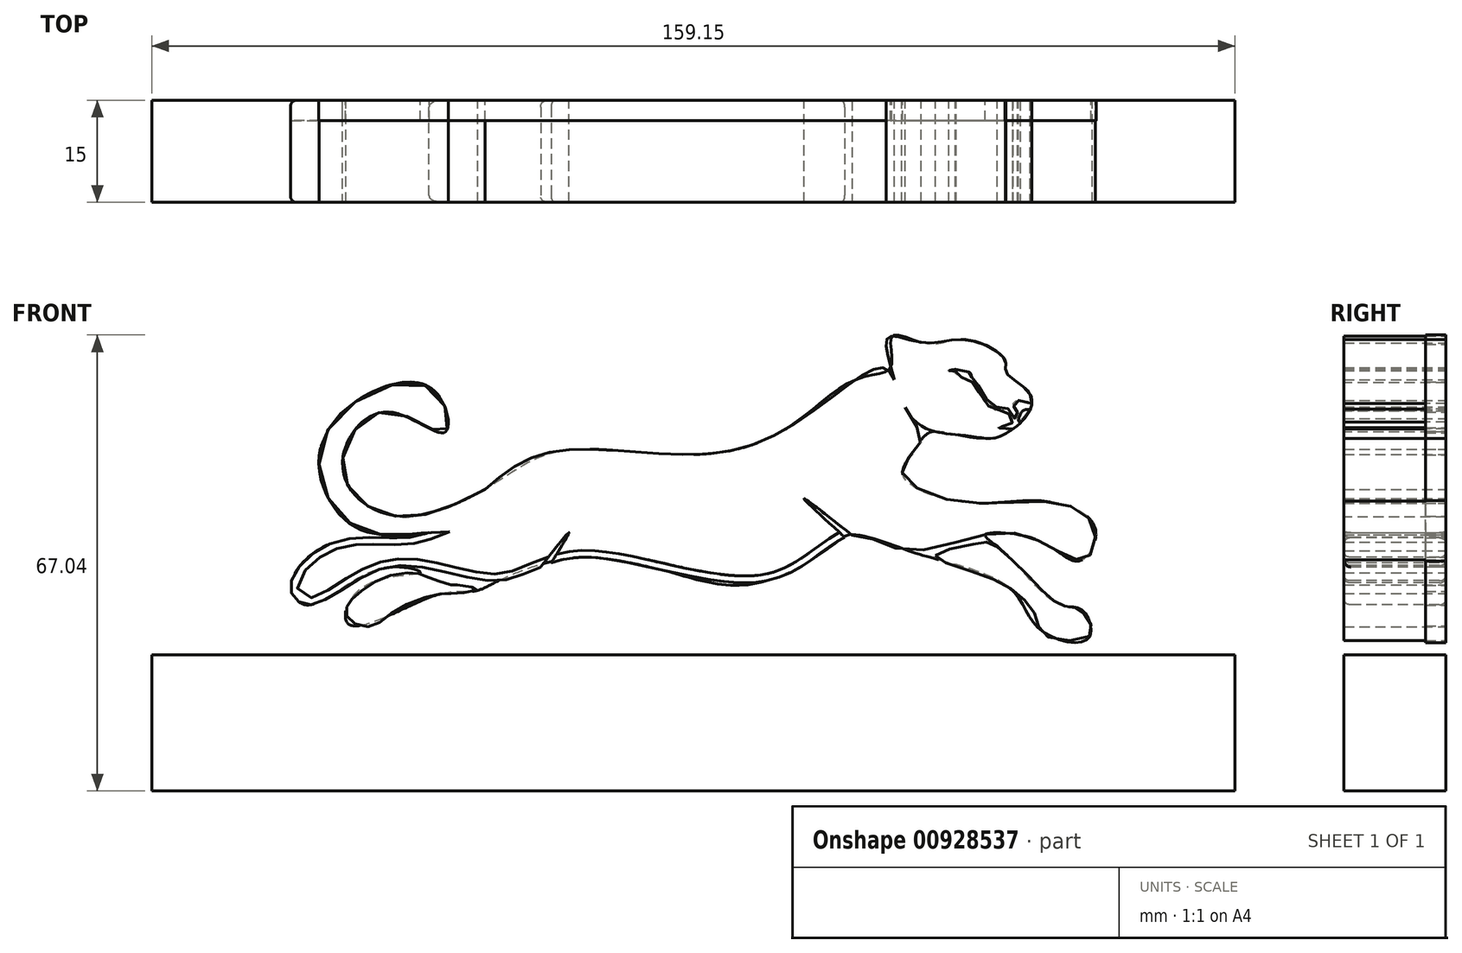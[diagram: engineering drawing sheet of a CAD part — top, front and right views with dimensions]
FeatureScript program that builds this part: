
annotation { "Feature Type Name" : "Feature", "Feature Type Description" : "" }
export const myFeature = defineFeature(function(context is Context, id is Id, definition is map)
    precondition{}
    {
        {
            var Q0;
            Q0=qCreatedBy(makeId("Front.planeOp"),FACE);
            var sketch = newSketch(context, id + "F0", { "sketchPlane" : qUnion([Q0])});
            skFitSpline(sketch, "E0", {"points": [v(-30.14, 6.91) * mm, v(-9.5, 13.73) * mm, v(10.97, 13.73) * mm, v(29.59, 25.16) * mm], "startDerivative": vector(60.52, 28) * mm, "endDerivative": vector(53.1, 44.41) * mm});
            skFitSpline(sketch, "E1", {"points": [v(-23.36, 10.05) * mm, v(-23.36, 18.53) * mm], "startDerivative": vector(0, 8.47) * mm, "endDerivative": vector(0, 8.47) * mm});
            skFitSpline(sketch, "E2", {"points": [v(-49.89, 46.42) * mm, v(-49.56, 44.66) * mm, v(-46.34, 43.56) * mm, v(-42.72, 45.94) * mm, v(-36.2, 48.35) * mm, v(-33.46, 48.44) * mm, v(-30.66, 49.06) * mm, v(-33.89, 49.68) * mm, v(-34.5, 49.68) * mm, v(-38.22, 50.92) * mm, v(-39.23, 51.35) * mm, v(-43.76, 50.99) * mm, v(-48.52, 48.12) * mm, v(-49.89, 46.42) * mm]});
            skFitSpline(sketch, "E3", {"points": [v(36.64, 53.99) * mm, v(42.67, 55.74) * mm, v(44.7, 55.84) * mm, v(49.12, 52.16) * mm, v(53.56, 47.7) * mm, v(55.7, 46.55) * mm, v(57.56, 46.13) * mm, v(59.06, 44.6) * mm, v(59.36, 42.25) * mm, v(52.87, 42.16) * mm, v(51.47, 44.8) * mm, v(48.86, 48.28) * mm, v(42.54, 51.48) * mm, v(36.64, 53.99) * mm]});
            skFitSpline(sketch, "E4", {"points": [v(33.12, 74.32) * mm, v(36.53, 72.22) * mm, v(38.89, 71.86) * mm, v(42.9, 71.37) * mm, v(46.39, 71.64) * mm, v(50.76, 77.12) * mm, v(47.05, 80.84) * mm, v(46.88, 82.64) * mm, v(41.24, 85.71) * mm, v(34.89, 85.28) * mm, v(29.8, 86.14) * mm, v(29.88, 82.45) * mm, v(33.12, 74.32) * mm]});
            skFitSpline(sketch, "E5", {"points": [v(-21.82, 68.7) * mm, v(-37.78, 57.37) * mm, v(-51.21, 56.12) * mm, v(-58.13, 49.3) * mm, v(-55.2, 46.78) * mm, v(-43.72, 52.32) * mm, v(-27.8, 50.3) * mm, v(-15.78, 53.72) * mm, v(12.22, 50.35) * mm, v(24.46, 57.02) * mm, v(32.14, 54.76) * mm, v(46.2, 57.38) * mm, v(54.33, 54.82) * mm, v(58.74, 53.54) * mm, v(59.97, 57.95) * mm, v(54.5, 61.77) * mm, v(39.58, 61.98) * mm, v(31.68, 66.7) * mm, v(34.46, 70.73) * mm, v(32.16, 75.8) * mm, v(28.94, 81.6) * mm, v(9.45, 70.15) * mm, v(-21.82, 68.7) * mm]});
            skFitSpline(sketch, "E6", {"points": [v(-37.78, 57.37) * mm, v(-48.49, 58.19) * mm, v(-53.07, 71.66) * mm, v(-37.62, 78.63) * mm, v(-35.47, 72.24) * mm, v(-44.01, 75.2) * mm, v(-50.52, 66.73) * mm, v(-42.68, 59.76) * mm, v(-29.54, 63.73) * mm], "startDerivative": vector(-59.25, -2.75) * mm, "endDerivative": vector(96.38, 50.14) * mm});
            skSolve(sketch);
        }
        {
            var Q0;
            Q0 = qSketchRegion(id + "F0", true);
            extrude(context, id + "F1", {"entities" : qUnion([Q0]), "depth" : 15 * mm, "offsetDistance" : 25 * mm});
        }
        {
            var Q0;
            Q0=makeQuery(id+"F1.opExtrude","CAP_FACE",FACE,{"disambiguationData":[OSD([sQuery(id+"F0.wireOp",EDGE,"E4"),sQuery(id+"F0.wireOp",EDGE,"E5"),sQuery(id+"F0.wireOp",EDGE,"E6")])],"isStart":false});
            var sketch = newSketch(context, id + "F2", { "sketchPlane" : qUnion([Q0])});
            skFitSpline(sketch, "E7", {"points": [v(23.3, 56.67) * mm, v(17.32, 62.35) * mm, v(24.37, 57) * mm], "startDerivative": vector(-18.57, 17) * mm, "endDerivative": vector(20.48, -16.14) * mm});
            skFitSpline(sketch, "E8", {"points": [v(-21.37, 52.3) * mm, v(-17.21, 57.37) * mm, v(-19.84, 52.9) * mm], "startDerivative": vector(11.4, 14.66) * mm, "endDerivative": vector(-8.73, -14.04) * mm});
            skFitSpline(sketch, "E9", {"points": [v(47.94, 72.62) * mm, v(45.71, 72.72) * mm, v(47.05, 73.16) * mm, v(48, 73.67) * mm, v(46.85, 75.3) * mm, v(45.11, 75.43) * mm, v(42.75, 78.49) * mm, v(41.54, 79.82) * mm, v(39.55, 80.78) * mm, v(39.66, 81.15) * mm, v(38.6, 81.14) * mm, v(39.83, 81.35) * mm, v(41.8, 80.74) * mm, v(41.91, 80.33) * mm, v(43.02, 78.86) * mm, v(45.13, 75.93) * mm, v(47.23, 75.63) * mm, v(48.39, 74.09) * mm, v(48.71, 75) * mm, v(48.22, 75.8) * mm, v(48.25, 76.6) * mm, v(50.76, 76.34) * mm, v(50.48, 75.5) * mm, v(49.64, 75.39) * mm, v(48.84, 74) * mm, v(49.05, 73.6) * mm], "startDerivative": vector(-25.97, 20.1) * mm, "endDerivative": vector(20.37, -8.25) * mm});
            skSolve(sketch);
        }
        {
            var Q0;
            Q0 = qSketchRegion(id + "F2", true);
            var Q1;
            {var subQ0=sQuery(id+"F2.wireOp",EDGE,"E9");var subQ1=makeQuery(id+"F1.opExtrude","CAP_EDGE",EDGE,{"disambiguationData":[OSD([sQuery(id+"F0.wireOp",EDGE,"E4")])],"isStart":false});var subQ2=makeQuery(id+"F2.imprint","INTERSECT",VERTEX,{"disambiguationData":[OD(0.0)],"derivedFrom":[subQ1,subQ0]});Q1=makeQuery(id+"F2.imprint","IMPRINT",FACE,{"disambiguationData":[TD([[makeQuery(id+"F2.imprint","IMPRINT",EDGE,{"disambiguationData":[TD([[subQ2,-1.0]])],"derivedFrom":subQ0}),-1.0]])]});}
            var Q2;
            {var subQ0=sQuery(id+"F2.wireOp",EDGE,"E7");Q2=makeQuery(id+"F2.imprint","IMPRINT",FACE,{"disambiguationData":[TD([[makeQuery(id+"F2.imprint","IMPRINT",EDGE,{"derivedFrom":subQ0}),-1.0]])]});}
            var Q3;
            {var subQ0=sQuery(id+"F2.wireOp",EDGE,"E8");Q3=makeQuery(id+"F2.imprint","IMPRINT",FACE,{"disambiguationData":[TD([[makeQuery(id+"F2.imprint","IMPRINT",EDGE,{"derivedFrom":subQ0}),-1.0]])]});}
            extrude(context, id + "F3", {"entities" : qUnion([Q0, Q1, Q2, Q3]), "operationType" : NewBodyOperationType.REMOVE, "oppositeDirection" : true, "depth" : 15 * mm, "offsetDistance" : 25 * mm});
        }
        {
            var Q0;
            {var subQ0=sQuery(id+"F0.wireOp",EDGE,"E6");var subQ1=sQuery(id+"F0.wireOp",EDGE,"E5");var subQ2=sQuery(id+"F0.wireOp",EDGE,"E4");var subQ3=makeQuery(id+"F0.imprint","IMPRINT",EDGE,{"disambiguationData":[TD([[makeQuery(id+"F0.imprint","INTERSECT",VERTEX,{"disambiguationData":[OD(0.0)],"derivedFrom":[subQ1,subQ0]}),-1.0]])],"derivedFrom":subQ1});Q0=makeQuery(id+"F3.boolean.opBoolean","SPLIT",EDGE,{"disambiguationData":[TD([makeQuery(id+"F1.opExtrude","CAP_FACE",FACE,{"disambiguationData":[OSD([subQ2,subQ1,subQ0])],"isStart":false}),makeQuery(id+"F1.opExtrude","SWEPT_FACE",FACE,{"disambiguationData":[OSD([subQ1]),TDD([subQ3])]}),makeQuery(id+"F3.opExtrude","SWEPT_FACE",FACE,{"disambiguationData":[OSD([sQuery(id+"F2.wireOp",EDGE,"E7")])]}),makeQuery(id+"F3.opExtrude","SWEPT_FACE",FACE,{"disambiguationData":[OSD([sQuery(id+"F2.wireOp",EDGE,"E8")])]})])],"derivedFrom":makeQuery(id+"F1.opExtrude","CAP_EDGE",EDGE,{"disambiguationData":[OSD([subQ1]),TDD([subQ3])],"isStart":false})});}
            var Q1;
            {var subQ0=sQuery(id+"F2.wireOp",EDGE,"E8");var subQ1=sQuery(id+"F0.wireOp",EDGE,"E5");Q1=makeQuery(id+"F3.boolean.opBoolean","COPY",EDGE,{"derivedFrom":makeQuery(id+"F3.opExtrude","SWEPT_EDGE",EDGE,{"disambiguationData":[OSD([subQ1,subQ0]),TDD([makeQuery(id+"F2.imprint","INTERSECT",VERTEX,{"disambiguationData":[OD(1.0)],"derivedFrom":[makeQuery(id+"F1.opExtrude","CAP_EDGE",EDGE,{"disambiguationData":[OSD([subQ1]),TDD([makeQuery(id+"F0.imprint","IMPRINT",EDGE,{"disambiguationData":[TD([[makeQuery(id+"F0.imprint","INTERSECT",VERTEX,{"disambiguationData":[OD(0.0)],"derivedFrom":[subQ1,sQuery(id+"F0.wireOp",EDGE,"E6")]}),-1.0]])],"derivedFrom":subQ1})])],"isStart":false}),subQ0]})])]})});}
            var Q2;
            {var subQ0=sQuery(id+"F0.wireOp",EDGE,"E6");var subQ1=sQuery(id+"F0.wireOp",EDGE,"E5");var subQ2=sQuery(id+"F0.wireOp",EDGE,"E4");var subQ3=makeQuery(id+"F0.imprint","IMPRINT",EDGE,{"disambiguationData":[TD([[makeQuery(id+"F0.imprint","INTERSECT",VERTEX,{"disambiguationData":[OD(0.0)],"derivedFrom":[subQ1,subQ0]}),-1.0]])],"derivedFrom":subQ1});Q2=makeQuery(id+"F3.boolean.opBoolean","SPLIT",EDGE,{"disambiguationData":[TD([makeQuery(id+"F1.opExtrude","CAP_FACE",FACE,{"disambiguationData":[OSD([subQ2,subQ1,subQ0])],"isStart":false}),makeQuery(id+"F1.opExtrude","SWEPT_FACE",FACE,{"disambiguationData":[OSD([subQ1]),TDD([subQ3])]}),makeQuery(id+"F1.opExtrude","SWEPT_FACE",FACE,{"disambiguationData":[OSD([subQ0])]}),makeQuery(id+"F3.opExtrude","SWEPT_FACE",FACE,{"disambiguationData":[OSD([sQuery(id+"F2.wireOp",EDGE,"E8")])]})])],"derivedFrom":makeQuery(id+"F1.opExtrude","CAP_EDGE",EDGE,{"disambiguationData":[OSD([subQ1]),TDD([subQ3])],"isStart":false})});}
            var Q3;
            {var subQ0=sQuery(id+"F0.wireOp",EDGE,"E6");var subQ1=sQuery(id+"F0.wireOp",EDGE,"E5");var subQ2=sQuery(id+"F0.wireOp",EDGE,"E4");var subQ3=makeQuery(id+"F0.imprint","IMPRINT",EDGE,{"disambiguationData":[TD([[makeQuery(id+"F0.imprint","INTERSECT",VERTEX,{"disambiguationData":[OD(0.0)],"derivedFrom":[subQ1,subQ0]}),-1.0]])],"derivedFrom":subQ1});Q3=makeQuery(id+"F3.boolean.opBoolean","SPLIT",EDGE,{"disambiguationData":[TD([makeQuery(id+"F1.opExtrude","CAP_FACE",FACE,{"disambiguationData":[OSD([subQ2,subQ1,subQ0])],"isStart":true}),makeQuery(id+"F1.opExtrude","SWEPT_FACE",FACE,{"disambiguationData":[OSD([subQ1]),TDD([subQ3])]}),makeQuery(id+"F3.opExtrude","SWEPT_FACE",FACE,{"disambiguationData":[OSD([sQuery(id+"F2.wireOp",EDGE,"E7")])]}),makeQuery(id+"F3.opExtrude","SWEPT_FACE",FACE,{"disambiguationData":[OSD([sQuery(id+"F2.wireOp",EDGE,"E8")])]})])],"derivedFrom":makeQuery(id+"F1.opExtrude","CAP_EDGE",EDGE,{"disambiguationData":[OSD([subQ1]),TDD([subQ3])],"isStart":true})});}
            var Q4;
            {var subQ0=sQuery(id+"F2.wireOp",EDGE,"E7");var subQ1=sQuery(id+"F0.wireOp",EDGE,"E5");Q4=makeQuery(id+"F3.boolean.opBoolean","COPY",EDGE,{"derivedFrom":makeQuery(id+"F3.opExtrude","SWEPT_EDGE",EDGE,{"disambiguationData":[OSD([subQ1,subQ0]),TDD([makeQuery(id+"F2.imprint","INTERSECT",VERTEX,{"disambiguationData":[OD(0.0)],"derivedFrom":[makeQuery(id+"F1.opExtrude","CAP_EDGE",EDGE,{"disambiguationData":[OSD([subQ1]),TDD([makeQuery(id+"F0.imprint","IMPRINT",EDGE,{"disambiguationData":[TD([[makeQuery(id+"F0.imprint","INTERSECT",VERTEX,{"disambiguationData":[OD(0.0)],"derivedFrom":[subQ1,sQuery(id+"F0.wireOp",EDGE,"E6")]}),-1.0]])],"derivedFrom":subQ1})])],"isStart":false}),subQ0]})])]})});}
            var Q5;
            {var subQ0=sQuery(id+"F0.wireOp",EDGE,"E6");var subQ1=sQuery(id+"F0.wireOp",EDGE,"E5");var subQ2=sQuery(id+"F0.wireOp",EDGE,"E4");var subQ3=makeQuery(id+"F0.imprint","IMPRINT",EDGE,{"disambiguationData":[TD([[makeQuery(id+"F0.imprint","INTERSECT",VERTEX,{"disambiguationData":[OD(0.0)],"derivedFrom":[subQ1,subQ0]}),-1.0]])],"derivedFrom":subQ1});Q5=makeQuery(id+"F3.boolean.opBoolean","SPLIT",EDGE,{"disambiguationData":[TD([makeQuery(id+"F1.opExtrude","CAP_FACE",FACE,{"disambiguationData":[OSD([subQ2,subQ1,subQ0])],"isStart":true}),makeQuery(id+"F1.opExtrude","SWEPT_FACE",FACE,{"disambiguationData":[OSD([subQ1]),TDD([subQ3])]}),makeQuery(id+"F1.opExtrude","SWEPT_FACE",FACE,{"disambiguationData":[OSD([subQ0])]}),makeQuery(id+"F3.opExtrude","SWEPT_FACE",FACE,{"disambiguationData":[OSD([sQuery(id+"F2.wireOp",EDGE,"E8")])]})])],"derivedFrom":makeQuery(id+"F1.opExtrude","CAP_EDGE",EDGE,{"disambiguationData":[OSD([subQ1]),TDD([subQ3])],"isStart":true})});}
            var Q6;
            {var subQ0=sQuery(id+"F2.wireOp",EDGE,"E7");var subQ1=sQuery(id+"F0.wireOp",EDGE,"E5");Q6=makeQuery(id+"F3.boolean.opBoolean","COPY",EDGE,{"derivedFrom":makeQuery(id+"F3.opExtrude","SWEPT_EDGE",EDGE,{"disambiguationData":[OSD([subQ1,subQ0]),TDD([makeQuery(id+"F2.imprint","INTERSECT",VERTEX,{"disambiguationData":[OD(1.0)],"derivedFrom":[makeQuery(id+"F1.opExtrude","CAP_EDGE",EDGE,{"disambiguationData":[OSD([subQ1]),TDD([makeQuery(id+"F0.imprint","IMPRINT",EDGE,{"disambiguationData":[TD([[makeQuery(id+"F0.imprint","INTERSECT",VERTEX,{"disambiguationData":[OD(0.0)],"derivedFrom":[subQ1,sQuery(id+"F0.wireOp",EDGE,"E6")]}),-1.0]])],"derivedFrom":subQ1})])],"isStart":false}),subQ0]})])]})});}
            var Q7;
            {var subQ0=sQuery(id+"F2.wireOp",EDGE,"E8");var subQ1=sQuery(id+"F0.wireOp",EDGE,"E5");Q7=makeQuery(id+"F3.boolean.opBoolean","COPY",EDGE,{"derivedFrom":makeQuery(id+"F3.opExtrude","SWEPT_EDGE",EDGE,{"disambiguationData":[OSD([subQ1,subQ0]),TDD([makeQuery(id+"F2.imprint","INTERSECT",VERTEX,{"disambiguationData":[OD(0.0)],"derivedFrom":[makeQuery(id+"F1.opExtrude","CAP_EDGE",EDGE,{"disambiguationData":[OSD([subQ1]),TDD([makeQuery(id+"F0.imprint","IMPRINT",EDGE,{"disambiguationData":[TD([[makeQuery(id+"F0.imprint","INTERSECT",VERTEX,{"disambiguationData":[OD(0.0)],"derivedFrom":[subQ1,sQuery(id+"F0.wireOp",EDGE,"E6")]}),-1.0]])],"derivedFrom":subQ1})])],"isStart":false}),subQ0]})])]})});}
            fillet(context, id + "F4", {"entities" : qUnion([Q0, Q1, Q2, Q3, Q4, Q5, Q6, Q7]), "radius" : 1 * mm, "rho" : 0.5, "crossSection" : FilletCrossSection.CONIC, "allowEdgeOverflow" : false});
        }
        {
            var Q0;
            Q0=qCreatedBy(makeId("Front.planeOp"),FACE);
            var sketch = newSketch(context, id + "F5", { "sketchPlane" : qUnion([Q0])});
            skLineSegment(sketch, "E10.bottom", {"start": v(-78.5, 39.38) * mm, "end": v(80.65, 39.38) * mm});
            skLineSegment(sketch, "E10.top", {"start": v(-78.5, 19.38) * mm, "end": v(80.65, 19.38) * mm});
            skLineSegment(sketch, "E10.left", {"start": v(-78.5, 39.38) * mm, "end": v(-78.5, 19.38) * mm});
            skLineSegment(sketch, "E10.right", {"start": v(80.65, 39.38) * mm, "end": v(80.65, 19.38) * mm});
            skSolve(sketch);
        }
        {
            var Q0;
            Q0=makeQuery(id+"F5.imprint","IMPRINT",FACE,{"disambiguationData":[TD([[makeQuery(id+"F5.imprint","IMPRINT",EDGE,{"derivedFrom":sQuery(id+"F5.wireOp",EDGE,"E10.bottom")}),-1.0]])]});
            var Q1;
            Q1 = qSketchRegion(id + "F7", true);
            extrude(context, id + "F6", {"entities" : qUnion([Q0, Q1]), "depth" : 15 * mm, "offsetDistance" : 25 * mm});
        }
        {
            var Q0;
            {var subQ0=sQuery(id+"F0.wireOp",EDGE,"E5");var subQ1=sQuery(id+"F0.wireOp",EDGE,"E4");var subQ2=makeQuery(id+"F0.imprint","INTERSECT",VERTEX,{"disambiguationData":[OD(0.0)],"derivedFrom":[subQ1,subQ0]});Q0=makeQuery(id+"F0.imprint","IMPRINT",FACE,{"disambiguationData":[TD([[makeQuery(id+"F0.imprint","IMPRINT",EDGE,{"disambiguationData":[TD([[subQ2,1.0]])],"derivedFrom":subQ1}),-1.0]])]});}
            var sketch = newSketch(context, id + "F7", { "sketchPlane" : qUnion([Q0])});
            skFitSpline(sketch, "E11", {"points": [v(-35.43, 72.12) * mm, v(-37, 78.23) * mm, v(-47.33, 77.41) * mm, v(-53.92, 68.7) * mm, v(-50.63, 59.74) * mm, v(-43.48, 57) * mm, v(-37.7, 57.36) * mm, v(-41.85, 56.67) * mm, v(-47.55, 56.58) * mm, v(-53.82, 54.97) * mm, v(-58.02, 49.5) * mm, v(-55.56, 46.71) * mm, v(-44.9, 52.06) * mm, v(-39.08, 51.45) * mm, v(-47.51, 49.33) * mm, v(-49.49, 43.84) * mm, v(-36.37, 48.27) * mm, v(-31.11, 48.75) * mm, v(-27.8, 50.17) * mm, v(-16.76, 53.63) * mm, v(-3.07, 51.78) * mm, v(10.1, 49.86) * mm, v(21.71, 55.67) * mm, v(24.46, 57.08) * mm, v(32.18, 54.86) * mm, v(37.44, 53.3) * mm, v(47.82, 48.98) * mm, v(52.13, 43.02) * mm, v(59.14, 41.82) * mm, v(58.22, 45.96) * mm, v(54.84, 46.76) * mm, v(46.4, 54.77) * mm, v(43.97, 57.07) * mm, v(51.97, 56.12) * mm, v(57.83, 53.22) * mm, v(60.13, 57.87) * mm, v(52.89, 61.98) * mm, v(40.93, 61.78) * mm, v(31.9, 65.73) * mm, v(33.57, 69.5) * mm, v(36.2, 72.21) * mm, v(45.36, 71.42) * mm, v(50.73, 77.24) * mm, v(46.91, 80.95) * mm, v(46.87, 82.7) * mm, v(40.85, 85.76) * mm, v(35.6, 85.09) * mm, v(30.26, 86.24) * mm, v(30.1, 81.82) * mm, v(25.24, 79.99) * mm, v(13.92, 72.14) * mm, v(-2.01, 68.83) * mm, v(-19.03, 69.23) * mm, v(-29.46, 63.81) * mm, v(-43.74, 60.01) * mm, v(-50.5, 67.52) * mm, v(-44, 75.09) * mm, v(-35.43, 72.12) * mm]});
            skSolve(sketch);
        }
        {
            var Q0;
            Q0 = qSketchRegion(id + "F7", true);
            extrude(context, id + "F8", {"entities" : qUnion([Q0]), "depth" : 3 * mm, "offsetDistance" : 25 * mm});
        }
    });
